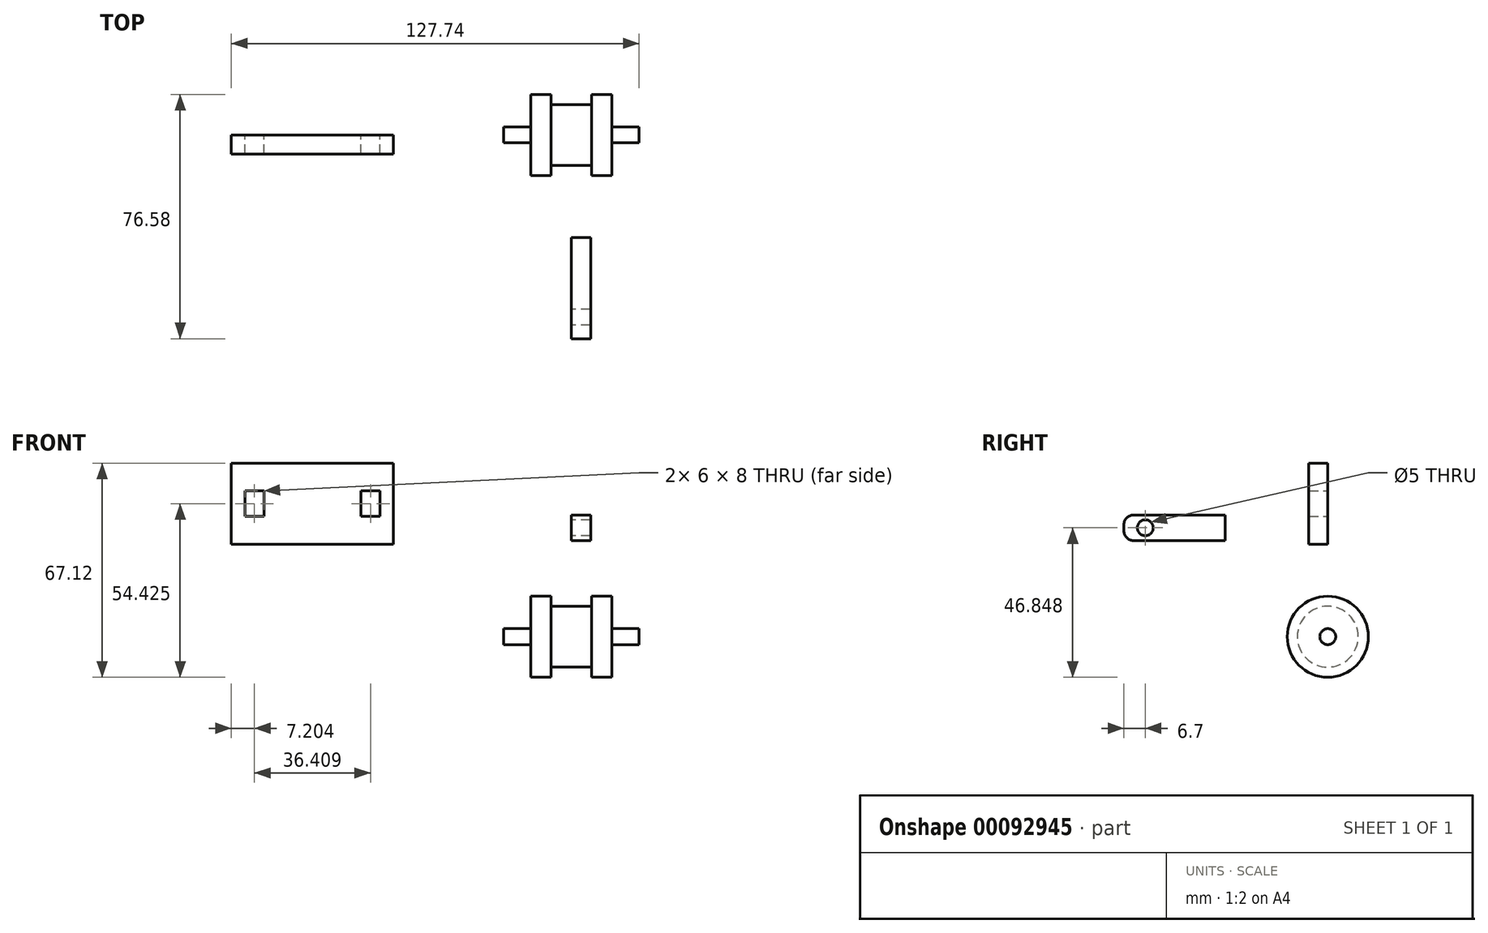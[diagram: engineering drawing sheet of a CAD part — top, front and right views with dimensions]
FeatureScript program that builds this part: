
annotation { "Feature Type Name" : "Feature", "Feature Type Description" : "" }
export const myFeature = defineFeature(function(context is Context, id is Id, definition is map)
    precondition{}
    {
        {
            var Q0;
            Q0=qCreatedBy(makeId("Right.planeOp"),FACE);
            var sketch = newSketch(context, id + "F0", { "sketchPlane" : qUnion([Q0])});
            skCircle(sketch, "E0", {"center": v(0, 0) * mm, "radius": 12.7 * mm});
            skCircle(sketch, "E1", {"center": v(0, 0) * mm, "radius": 9.53 * mm});
            skCircle(sketch, "E2", {"center": v(0, 0) * mm, "radius": 2.5 * mm});
            skSolve(sketch);
        }
        {
            var Q0;
            Q0=makeQuery(id+"F0.imprint","IMPRINT",FACE,{"disambiguationData":[TD([[makeQuery(id+"F0.imprint","IMPRINT",EDGE,{"derivedFrom":sQuery(id+"F0.wireOp",EDGE,"E2")}),1.0]])]});
            extrude(context, id + "F1", {"entities" : qUnion([Q0]), "endBound" : BoundingType.SYMMETRIC, "depth" : 25.4 * mm + 12 * mm + 5 * mm});
        }
        {
            var Q0;
            Q0=makeQuery(id+"F0.imprint","IMPRINT",FACE,{"disambiguationData":[TD([[makeQuery(id+"F0.imprint","IMPRINT",EDGE,{"derivedFrom":sQuery(id+"F0.wireOp",EDGE,"E0")}),1.0]])]});
            var Q1;
            Q1=makeQuery(id+"F0.imprint","IMPRINT",FACE,{"disambiguationData":[TD([[makeQuery(id+"F0.imprint","IMPRINT",EDGE,{"derivedFrom":sQuery(id+"F0.wireOp",EDGE,"E1")}),1.0]])]});
            extrude(context, id + "F2", {"entities" : qUnion([Q0, Q1]), "operationType" : NewBodyOperationType.ADD, "endBound" : BoundingType.SYMMETRIC, "depth" : 25.4 * mm});
        }
        {
            var Q0;
            Q0 = qSketchRegion(id + "F0", true);
            extrude(context, id + "F3", {"entities" : qUnion([Q0]), "operationType" : NewBodyOperationType.REMOVE, "endBound" : BoundingType.SYMMETRIC, "oppositeDirection" : true, "depth" : 12.7 * mm});
        }
        {
            var Q0;
            Q0=qCreatedBy(makeId("Right.planeOp"),FACE);
            var sketch = newSketch(context, id + "F4", { "sketchPlane" : qUnion([Q0])});
            skLineSegment(sketch, "E3.bottom", {"start": v(-32.13, 30.15) * mm, "end": v(-60.88, 30.15) * mm});
            skLineSegment(sketch, "E3.top", {"start": v(-32.13, 38.15) * mm, "end": v(-60.88, 38.15) * mm});
            skLineSegment(sketch, "E3.left", {"start": v(-32.13, 30.15) * mm, "end": v(-32.13, 38.15) * mm});
            skLineSegment(sketch, "E3.right", {"start": v(-63.88, 33.15) * mm, "end": v(-63.88, 35.15) * mm});
            skPoint(sketch, "E3.middle", {"position": v(-48, 34.15) * mm});
            skCircle(sketch, "E4", {"center": v(-57.18, 34.15) * mm, "radius": 2.5 * mm});
            skPoint(sketch, "E5.visualSharp", {"position": v(-63.88, 38.15) * mm});
            skArc(sketch, "E5.filletArc", {"start": v(-60.88, 38.15) * mm, "mid": v(-63, 37.27) * mm, "end": v(-63.88, 35.15) * mm});
            skPoint(sketch, "E6.visualSharp", {"position": v(-63.88, 30.15) * mm});
            skArc(sketch, "E6.filletArc", {"start": v(-63.88, 33.15) * mm, "mid": v(-63, 31.03) * mm, "end": v(-60.88, 30.15) * mm});
            skSolve(sketch);
        }
        {
            var Q0;
            Q0 = qSketchRegion(id + "F4", true);
            extrude(context, id + "F5", {"entities" : qUnion([Q0]), "depth" : 6 * mm});
        }
        {
            var Q0;
            Q0=qCreatedBy(makeId("Front.planeOp"),FACE);
            var sketch = newSketch(context, id + "F6", { "sketchPlane" : qUnion([Q0])});
            skLineSegment(sketch, "E7.bottom", {"start": v(-55.74, 29.02) * mm, "end": v(-106.54, 29.02) * mm});
            skLineSegment(sketch, "E7.top", {"start": v(-55.74, 54.42) * mm, "end": v(-106.54, 54.42) * mm});
            skLineSegment(sketch, "E7.left", {"start": v(-55.74, 29.02) * mm, "end": v(-55.74, 54.42) * mm});
            skLineSegment(sketch, "E7.right", {"start": v(-106.54, 29.02) * mm, "end": v(-106.54, 54.42) * mm});
            skPoint(sketch, "E7.middle", {"position": v(-81.14, 41.72) * mm});
            skLineSegment(sketch, "E8.bottom", {"start": v(-96.34, 37.72) * mm, "end": v(-102.34, 37.72) * mm});
            skLineSegment(sketch, "E8.top", {"start": v(-96.34, 45.72) * mm, "end": v(-102.34, 45.72) * mm});
            skLineSegment(sketch, "E8.left", {"start": v(-96.34, 37.72) * mm, "end": v(-96.34, 45.72) * mm});
            skLineSegment(sketch, "E8.right", {"start": v(-102.34, 37.72) * mm, "end": v(-102.34, 45.72) * mm});
            skPoint(sketch, "E8.middle", {"position": v(-99.34, 41.72) * mm});
            skLineSegment(sketch, "E9.bottom", {"start": v(-59.93, 37.72) * mm, "end": v(-65.93, 37.72) * mm});
            skLineSegment(sketch, "E9.top", {"start": v(-59.93, 45.72) * mm, "end": v(-65.93, 45.72) * mm});
            skLineSegment(sketch, "E9.left", {"start": v(-59.93, 37.72) * mm, "end": v(-59.93, 45.72) * mm});
            skLineSegment(sketch, "E9.right", {"start": v(-65.93, 37.72) * mm, "end": v(-65.93, 45.72) * mm});
            skPoint(sketch, "E9.middle", {"position": v(-62.93, 41.72) * mm});
            skSolve(sketch);
        }
        {
            var Q0;
            Q0 = qSketchRegion(id + "F6", true);
            extrude(context, id + "F7", {"entities" : qUnion([Q0]), "depth" : 6 * mm});
        }
    });
